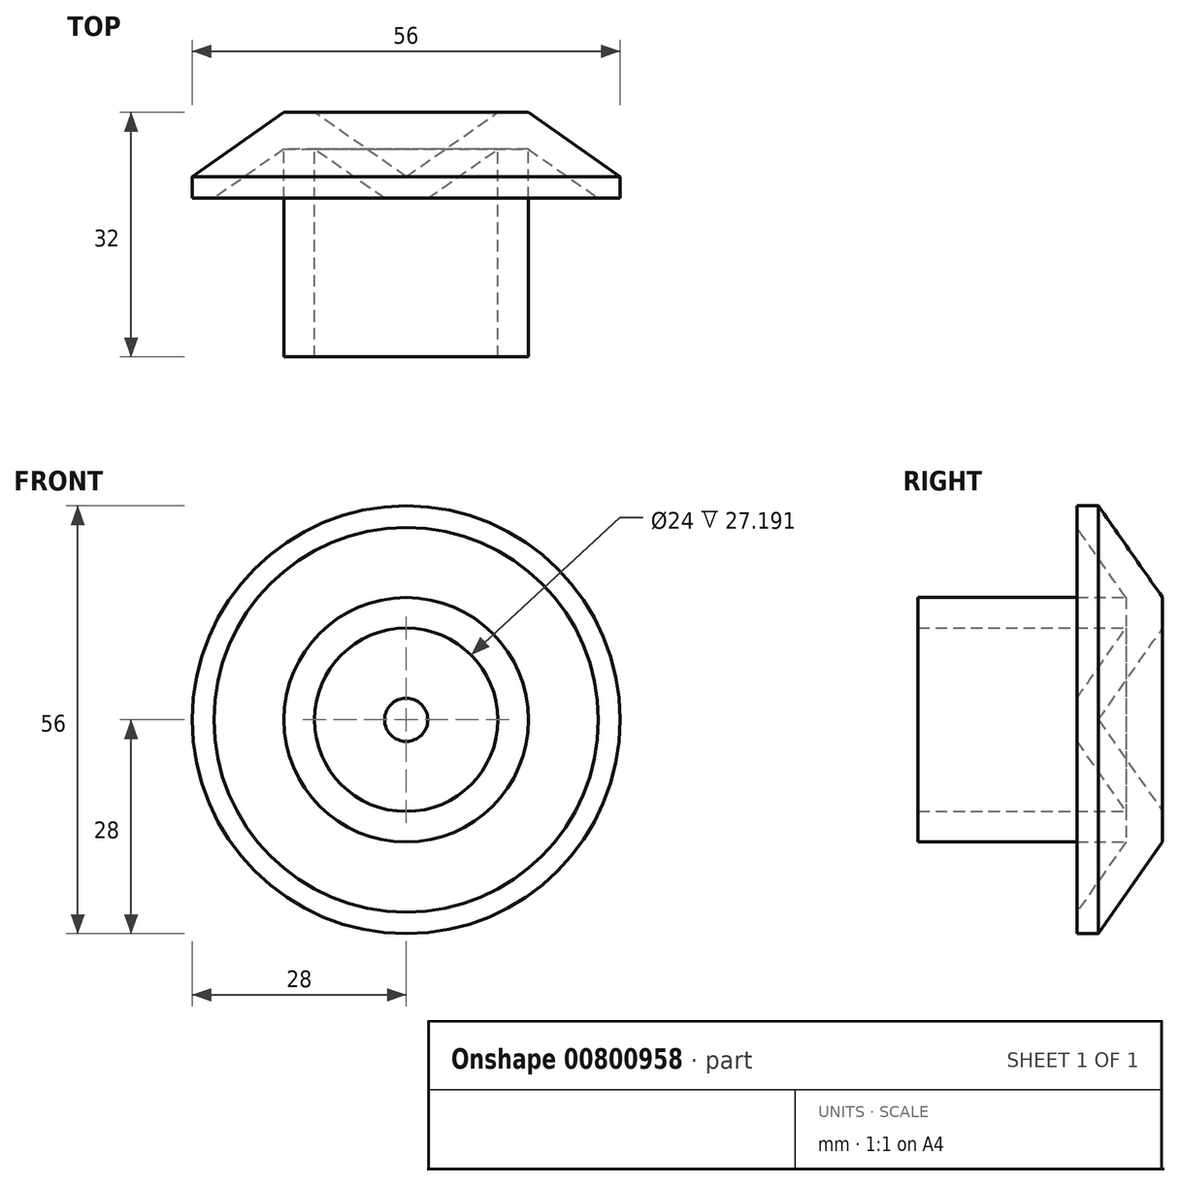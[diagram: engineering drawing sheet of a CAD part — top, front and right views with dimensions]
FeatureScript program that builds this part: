
annotation { "Feature Type Name" : "Feature", "Feature Type Description" : "" }
export const myFeature = defineFeature(function(context is Context, id is Id, definition is map)
    precondition{}
    {
        {
            var Q0;
            Q0=qCreatedBy(makeId("Top.planeOp"),FACE);
            var sketch = newSketch(context, id + "F0", { "sketchPlane" : qUnion([Q0])});
            skLineSegment(sketch, "E0", {"start": v(12, 0) * mm, "end": v(0, -8.4) * mm});
            skLineSegment(sketch, "E1", {"start": v(0, -8.4) * mm, "end": v(0, -11.23) * mm});
            skLineSegment(sketch, "E2", {"start": v(0, -11.23) * mm, "end": v(2.83, -11.23) * mm});
            skLineSegment(sketch, "E3", {"start": v(2.83, -11.23) * mm, "end": v(12, -4.8) * mm});
            skLineSegment(sketch, "E4", {"start": v(12, -4.8) * mm, "end": v(12, -32) * mm});
            skLineSegment(sketch, "E5", {"start": v(12, -32) * mm, "end": v(16, -32) * mm});
            skLineSegment(sketch, "E6", {"start": v(16, -32) * mm, "end": v(16, -4.8) * mm});
            skLineSegment(sketch, "E7", {"start": v(16, -4.8) * mm, "end": v(25.17, -11.23) * mm});
            skLineSegment(sketch, "E8", {"start": v(25.17, -11.23) * mm, "end": v(28, -11.23) * mm});
            skLineSegment(sketch, "E9", {"start": v(28, -11.23) * mm, "end": v(28, -8.4) * mm});
            skLineSegment(sketch, "E10", {"start": v(28, -8.4) * mm, "end": v(16, 0) * mm});
            skLineSegment(sketch, "E11", {"start": v(16, 0) * mm, "end": v(12, 0) * mm});
            skLineSegment(sketch, "E12", {"start": v(12, -4.8) * mm, "end": v(12, 0) * mm, "construction": true});
            skSolve(sketch);
        }
        {
            var Q0;
            Q0=makeQuery(id+"F0.imprint","IMPRINT",FACE,{"disambiguationData":[TD([[makeQuery(id+"F0.imprint","IMPRINT",EDGE,{"derivedFrom":sQuery(id+"F0.wireOp",EDGE,"E0")}),1.0]])]});
            var Q1;
            Q1=sQuery(id+"F0.wireOp",EDGE,"E1");
            revolve(context, id + "F1", {"surfaceOperationType" : NewSurfaceOperationType.NEW, "entities" : qUnion([Q0]), "axis" : qUnion([Q1]), "revolveType" : RevolveType.FULL});
        }
    });
